# Revit family: Hager-PABLO-Surface_mounted-IP65-With_Cover-Without_DIN-Hosted-IT-it
name_source: partatom
category: Electrical Equipment
units: mm (PartAtom-declared; Revit-internal decimal feet)

## family parameters
Cut with Voids When Loaded = No
Host = Face
Maintain Annotation Orientation = Yes
Panel Configuration = Two Columns, Circuits Across
Part Type = Panelboard
Room Calculation Point = No
Round Connector Dimension = Use Diameter
Shared = No

## types (11) — shared parameters
BC_MODEL_ID = 1554431
BC_OBJECT_ID = 513917
BC_OBJECT_VERSION = #6
Code hager = ADD-EC000214_EU
EF000003 - Tipo di montaggio = A parete
EF000024 - Resistente ai raggi UV = No
EF000116 - Numero RAL = 7035
EF000118 - Con piastra di montaggio = No
EF001062 - Esecuzione EMC = No
EF001088 - Possibilità di applicazione = No
EF001134 - Barra DIN = No
EF005474 - Grado di protezione (IP) = IP65
EF006306 - Con serratura = No
EF015776 - Morsettiera di terra = No
EF015777 - Morsettiera neutra = No
ETIM class code = EC000214
ETIM class name = Small distribution board
HG000001 - Numero di colonne = 1
HG000002-with door or cover-it = Yes
HG000003-Range-it = PABLO
HG000005-Thickness-it = 2 mm  [stored 0.00656168 ft]
HG000006-Flush mounted-it = No
HG000009-Double swing door-it = No
HG000010-Asymmetric doors-it = No
HG000011-Empty rows from bottom-it = No
HG000012-Door swing angle-it = 90.00°
HG000013-Door on the left-it = No
HG000014-Door on the right-it = Yes
HG000015-Clearance visibility-it = Yes
HG000016-Door 3D visibility-it = Yes
HG000017-Distance between poles-it = 18 mm  [stored 0.0590551 ft]
HG000060-RAL-number = 7035
HG000099-Onfly Template ID-it-IT = 507532
Manufacturer = Hager
Name = PABLO-Surface_mounted-IP65-With_Cover-Without_DIN-IT
Name BIM&CO = Electricity
Name hager = ADD_Enclosures_EC000214
Uniformat = Low Tension Service & Dist.
Uniformat code = D501001
zero-valued in all types: Default Elevation, EF000218 - Profondità di incasso, EF000332 - Altezza della parte incassata, EF001131 - Profondità interna, HG000007-Number of empty columns-it, HG000008-Number of empty rows-it

## per-type parameters (varying)
| type | BC_VARIANT_ID | EF000008 - Larghezza | EF000040 - Altezza | EF000049 - Profondità | EF000266 - Numero di file | EF000846 - Larghezza di montaggio | EF002950 - Numero moduli DIN | EF006244 - Coperchio/porta trasparente | EF015941 - Segnale di passaggio porta | HG000004-Manufacturer reference-it | HGEF000266-Numero di file | HGEF0002950-Numero moduli DIN |
| PABLO-Surface_mounted_W143_H210_D102_4_Modular_Spacing-B06521 | 1179103 | 143 mm | 210 mm  [stored 0.688976 ft] | 102 mm | 1 | 143 mm | 4 | Yes | Yes | B06521 | 1 | 4 |
| PABLO-Surface_mounted_W215_H210_D105_8_Modular_Spacing-B06522 | 1179104 | 215 mm | 210 mm  [stored 0.688976 ft] | 105 mm  [stored 0.344488 ft] | 1 | 215 mm | 8 | Yes | No | B06522 | 1 | 8 |
| PABLO-Surface_mounted_W314_H263_D143_12_Modular_Spacing-B06523 | 1179105 | 314 mm  [stored 1.03018 ft] | 263 mm  [stored 0.862861 ft] | 143 mm | 1 | 314 mm  [stored 1.03018 ft] | 12 | Yes | No | B06523 | 1 | 12 |
| PABLO-Surface_mounted_W426_H657_D148_19_Modular_Spacing-B06527 | 1179106 | 426 mm  [stored 1.39764 ft] | 657 mm | 148 mm  [stored 0.485564 ft] | 3 | 426 mm  [stored 1.39764 ft] | 19 | No | No | B06527 | 3 | 19 |
| PABLO-Surface_mounted_W143_H210_D102_4_Modular_Spacing-B06534 | 1179107 | 143 mm | 210 mm  [stored 0.688976 ft] | 102 mm | 1 | 0 mm  [stored 0 ft] | 4 | Yes | No | B06534 | 1 | 4 |
| PABLO-Surface_mounted_W215_H210_D105_8_Modular_Spacing-B06537 | 1179108 | 215 mm | 210 mm  [stored 0.688976 ft] | 105 mm  [stored 0.344488 ft] | 1 | 0 mm  [stored 0 ft] | 8 | Yes | No | B06537 | 1 | 8 |
| PABLO-Surface_mounted_W314_H263_D143_13_Modular_Spacing-B06540 | 1179109 | 314 mm  [stored 1.03018 ft] | 263 mm  [stored 0.862861 ft] | 143 mm | 1 | 0 mm  [stored 0 ft] | 13 | Yes | No | B06540 | 1 | 13 |
| PABLO-Surface_mounted_W314_H420_D143_12_Modular_Spacing-B06541 | 1179110 | 314 mm  [stored 1.03018 ft] | 420 mm  [stored 1.37795 ft] | 143 mm | 2 | 0 mm  [stored 0 ft] | 12 | Yes | No | B06541 | 2 | 12 |
| PABLO-Surface_mounted_W426_H288_D148_18_Modular_Spacing-B06542 | 1179111 | 426 mm  [stored 1.39764 ft] | 288 mm  [stored 0.944882 ft] | 148 mm  [stored 0.485564 ft] | 1 | 0 mm  [stored 0 ft] | 18 | Yes | No | B06542 | 1 | 18 |
| PABLO-Surface_mounted_W426_H470_D148_18_Modular_Spacing-B06543 | 1179112 | 426 mm  [stored 1.39764 ft] | 470 mm  [stored 1.54199 ft] | 148 mm  [stored 0.485564 ft] | 2 | 0 mm  [stored 0 ft] | 18 | No | No | B06543 | 2 | 18 |
| PABLO-Surface_mounted_W426_H657_D148_18_Modular_Spacing-B06544 | 1179113 | 426 mm  [stored 1.39764 ft] | 657 mm | 148 mm  [stored 0.485564 ft] | 3 | 0 mm  [stored 0 ft] | 18 | Yes | No | B06544 | 3 | 18 |

note: column(s) folded — value = type name in every type: Reference

note: [stored X ft] marks values corroborated as IEEE doubles in the binary element streams (Revit-internal decimal feet)

## geometry (parser evidence)
native form markers: Sweep x13
no freeform markers — native parametric forms only
